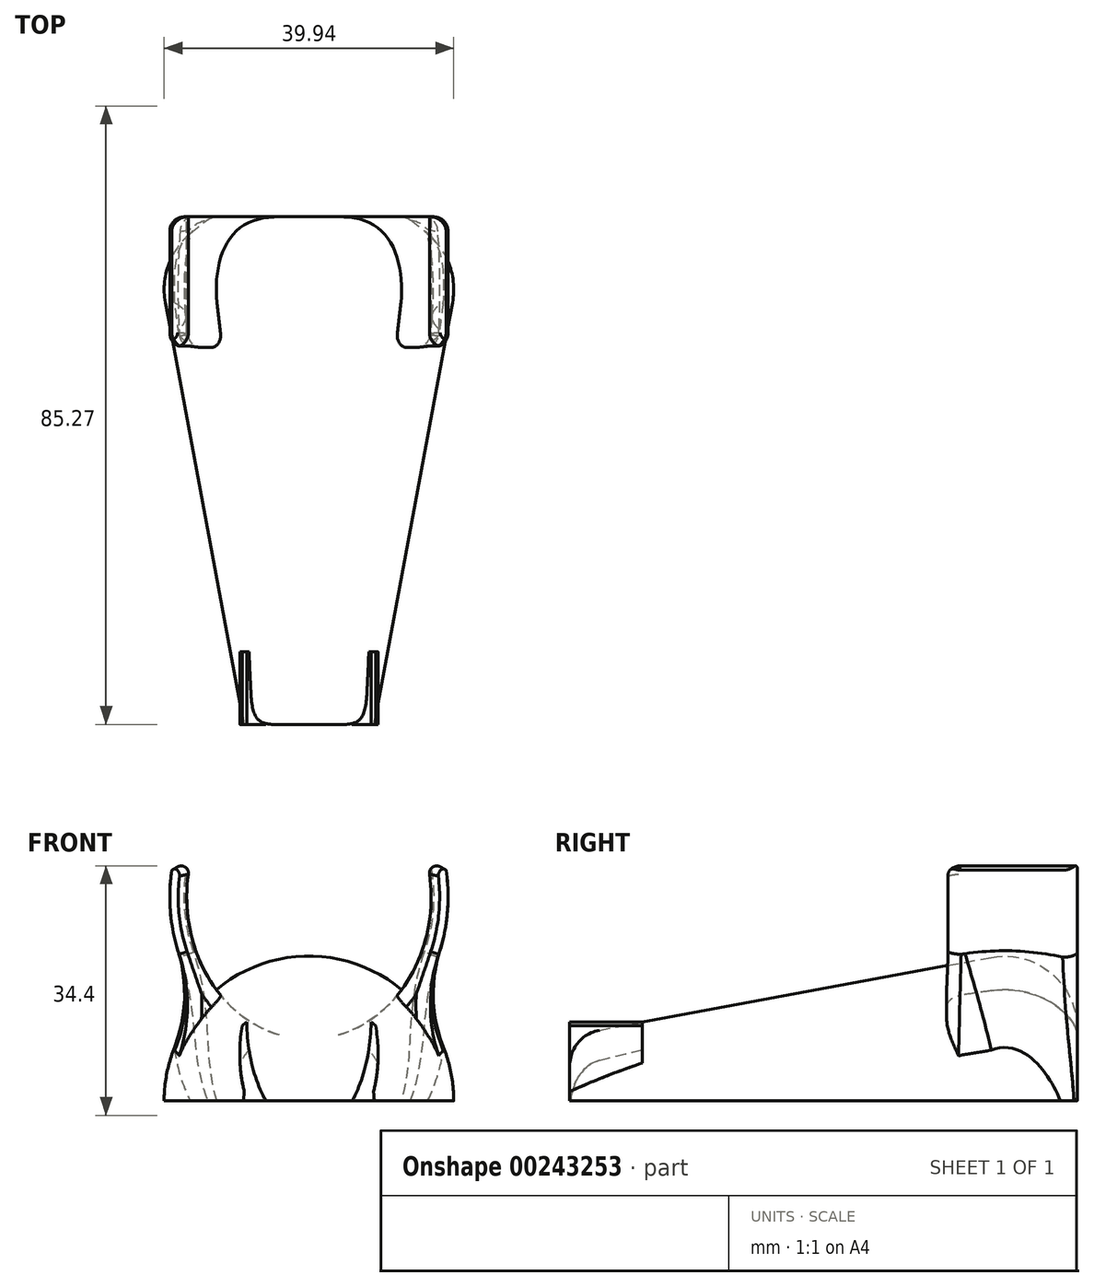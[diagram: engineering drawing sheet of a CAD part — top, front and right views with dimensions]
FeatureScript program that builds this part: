
annotation { "Feature Type Name" : "Feature", "Feature Type Description" : "" }
export const myFeature = defineFeature(function(context is Context, id is Id, definition is map)
    precondition{}
    {
        {
            var Q0;
            Q0=qCreatedBy(makeId("Right.planeOp"),FACE);
            var sketch = newSketch(context, id + "F0", { "sketchPlane" : qUnion([Q0])});
            skLineSegment(sketch, "E0", {"start": v(0, 0) * mm, "end": v(70, 0) * mm});
            skLineSegment(sketch, "E1", {"start": v(0, 0) * mm, "end": v(0, 9) * mm});
            skLineSegment(sketch, "E2", {"start": v(0, 9) * mm, "end": v(70, 22) * mm});
            skLineSegment(sketch, "E3", {"start": v(70, 22) * mm, "end": v(70, 0) * mm});
            skLineSegment(sketch, "E4", {"start": v(0, 0) * mm, "end": v(-40.56, 0) * mm, "construction": true});
            skSolve(sketch);
        }
        {
            var Q0;
            Q0 = qSketchRegion(id + "F0", true);
            var Q1;
            Q1=sQuery(id+"F0.wireOp",EDGE,"E4");
            revolve(context, id + "F1", {"entities" : qUnion([Q0]), "axis" : qUnion([Q1]), "revolveType" : RevolveType.SYMMETRIC, "angle" : 180 * degree});
        }
        {
            var Q0;
            Q0=makeQuery(id+"F1.opRevolve","SWEPT_FACE",FACE,{"disambiguationData":[OSD([sQuery(id+"F0.wireOp",EDGE,"E1")])]});
            var sketch = newSketch(context, id + "F2", { "sketchPlane" : qUnion([Q0])});
            skEllipticalArc(sketch, "E5", {});
            skEllipticalArc(sketch, "E6", {});
            skArc(sketch, "E7", {"start": v(-16.27, 33.26) * mm, "mid": v(-17.6, 32.57) * mm, "end": v(-18.92, 31.83) * mm});
            skArc(sketch, "E8.trimOffspring", {"start": v(18.92, 31.83) * mm, "mid": v(17.6, 32.57) * mm, "end": v(16.27, 33.26) * mm});
            const initialGuessF2  = {"E5": [0, 0.02812500111758709, 0, -1, 0.01959677506238222, 0.016858613568751533, 4.447179239963011, 1.8360060672165754], "E6": [0, 0.02812500111758709, 0, 1, 0.021955648437142372, 0.019191871203235133, 1.4012127593999653, 4.881972547779622]};
            skSetInitialGuess(sketch, initialGuessF2);
            skSolve(sketch);
        }
        {
            var Q0;
            Q0=makeQuery(id+"F1.opRevolve","SWEPT_FACE",FACE,{"disambiguationData":[OSD([sQuery(id+"F0.wireOp",EDGE,"E3")])]});
            var sketch = newSketch(context, id + "F3", { "sketchPlane" : qUnion([Q0])});
            skEllipticalArc(sketch, "E9.0", {});
            skEllipticalArc(sketch, "E9.1", {});
            skPoint(sketch, "E9.2", {"position": v(-16.27, 33.26) * mm});
            skPoint(sketch, "E9.3", {"position": v(-18.92, 31.83) * mm});
            skArc(sketch, "E9.4", {"start": v(-18.92, 31.83) * mm, "mid": v(-17.6, 32.57) * mm, "end": v(-16.27, 33.26) * mm});
            skArc(sketch, "E9.5", {"start": v(16.27, 33.26) * mm, "mid": v(17.6, 32.57) * mm, "end": v(18.92, 31.83) * mm});
            skPoint(sketch, "E9.6", {"position": v(-17.6, 32.57) * mm});
            const initialGuessF3  = {"E9.0": [0, 0.02812500111758709, 0, -1, 0.01959677506238222, 0.016858613568751533, 4.4471792399630115, 1.8360060672165759], "E9.1": [0, 0.02812500111758709, 0, 1, 0.021955648437142372, 0.019191871203235133, 1.4012127593999646, 4.881972547779621]};
            skSetInitialGuess(sketch, initialGuessF3);
            skSolve(sketch);
        }
        {
            var Q0;
            Q0 = qSketchRegion(id + "F3", true);
            extrude(context, id + "F4", {"entities" : qUnion([Q0]), "operationType" : NewBodyOperationType.ADD, "oppositeDirection" : true, "depth" : 18 * mm});
        }
        {
            var Q0;
            {var subQ0=sQuery(id+"F0.wireOp",EDGE,"E2");var subQ1=sQuery(id+"F0.wireOp",EDGE,"E3");var subQ2=sQuery(id+"F3.wireOp",EDGE,"E9.0");Q0=makeQuery(id+"F4.boolean.opBoolean","SPLIT",EDGE,{"disambiguationData":[TD([makeQuery(id+"F1.opRevolve","SWEPT_FACE",FACE,{"disambiguationData":[OSD([subQ0])]}),makeQuery(id+"F1.opRevolve","SWEPT_FACE",FACE,{"disambiguationData":[OSD([subQ1])]}),makeQuery(id+"F4.opExtrude","SWEPT_FACE",FACE,{"disambiguationData":[OSD([subQ2])]}),makeQuery(id+"F4.opExtrude","CAP_FACE",FACE,{"disambiguationData":[OSD([subQ2,sQuery(id+"F3.wireOp",EDGE,"E9.1"),sQuery(id+"F3.wireOp",EDGE,"E9.4"),sQuery(id+"F3.wireOp",EDGE,"E9.5")])],"isStart":true})])],"derivedFrom":makeQuery(id+"F1.opRevolve","SWEPT_EDGE",EDGE,{"disambiguationData":[OSD([subQ0,subQ1])]})});}
            var Q1;
            {var subQ0=sQuery(id+"F3.wireOp",EDGE,"E9.1");var subQ1=sQuery(id+"F0.wireOp",EDGE,"E3");var subQ2=sQuery(id+"F0.wireOp",EDGE,"E2");Q1=makeQuery(id+"F4.boolean.opBoolean","SPLIT",EDGE,{"disambiguationData":[TD([makeQuery(id+"F1.opRevolve","CAP_FACE",FACE,{"disambiguationData":[OSD([sQuery(id+"F0.wireOp",EDGE,"E0"),sQuery(id+"F0.wireOp",EDGE,"E1"),subQ2,subQ1])],"isStart":true}),makeQuery(id+"F1.opRevolve","SWEPT_FACE",FACE,{"disambiguationData":[OSD([subQ2])]}),makeQuery(id+"F1.opRevolve","SWEPT_FACE",FACE,{"disambiguationData":[OSD([subQ1])]}),makeQuery(id+"F4.opExtrude","CAP_FACE",FACE,{"disambiguationData":[OSD([sQuery(id+"F3.wireOp",EDGE,"E9.0"),subQ0,sQuery(id+"F3.wireOp",EDGE,"E9.4"),sQuery(id+"F3.wireOp",EDGE,"E9.5")])],"isStart":true}),makeQuery(id+"F4.opExtrude","SWEPT_FACE",FACE,{"disambiguationData":[OSD([subQ0])]})]),OD(0.0)],"derivedFrom":makeQuery(id+"F1.opRevolve","SWEPT_EDGE",EDGE,{"disambiguationData":[OSD([subQ2,subQ1])]})});}
            var Q2;
            {var subQ0=sQuery(id+"F3.wireOp",EDGE,"E9.1");var subQ1=sQuery(id+"F0.wireOp",EDGE,"E3");var subQ2=sQuery(id+"F0.wireOp",EDGE,"E2");Q2=makeQuery(id+"F4.boolean.opBoolean","SPLIT",EDGE,{"disambiguationData":[TD([makeQuery(id+"F1.opRevolve","CAP_FACE",FACE,{"disambiguationData":[OSD([sQuery(id+"F0.wireOp",EDGE,"E0"),sQuery(id+"F0.wireOp",EDGE,"E1"),subQ2,subQ1])],"isStart":true}),makeQuery(id+"F1.opRevolve","SWEPT_FACE",FACE,{"disambiguationData":[OSD([subQ2])]}),makeQuery(id+"F1.opRevolve","SWEPT_FACE",FACE,{"disambiguationData":[OSD([subQ1])]}),makeQuery(id+"F4.opExtrude","CAP_FACE",FACE,{"disambiguationData":[OSD([sQuery(id+"F3.wireOp",EDGE,"E9.0"),subQ0,sQuery(id+"F3.wireOp",EDGE,"E9.4"),sQuery(id+"F3.wireOp",EDGE,"E9.5")])],"isStart":true}),makeQuery(id+"F4.opExtrude","SWEPT_FACE",FACE,{"disambiguationData":[OSD([subQ0])]})]),OD(1.0)],"derivedFrom":makeQuery(id+"F1.opRevolve","SWEPT_EDGE",EDGE,{"disambiguationData":[OSD([subQ2,subQ1])]})});}
            fillet(context, id + "F5", {"entities" : qUnion([Q0, Q1, Q2]), "radius" : 10 * mm, "tangentPropagation" : true, "allowEdgeOverflow" : false});
        }
        {
            var Q0;
            Q0=makeQuery(id+"F1.opRevolve","SWEPT_FACE",FACE,{"disambiguationData":[OSD([sQuery(id+"F0.wireOp",EDGE,"E1")])]});
            var sketch = newSketch(context, id + "F6", { "sketchPlane" : qUnion([Q0])});
            skEllipticalArc(sketch, "E10", {});
            skPoint(sketch, "E10.centerSnap0", {"position": v(0, 9) * mm});
            skEllipticalArc(sketch, "E11", {});
            skArc(sketch, "E12", {"start": v(-8.6, 10.88) * mm, "mid": v(-8.9, 10.64) * mm, "end": v(-9.19, 10.38) * mm});
            skArc(sketch, "E13.trimOffspring", {"start": v(9.19, 10.38) * mm, "mid": v(8.9, 10.64) * mm, "end": v(8.6, 10.88) * mm});
            skArc(sketch, "E14", {"start": v(-6.72, 1.57) * mm, "mid": v(-7.7, 1) * mm, "end": v(-8.65, 0.34) * mm});
            skEllipticalArc(sketch, "E15.trimOffspring", {});
            skEllipticalArc(sketch, "E16.trimOffspring", {});
            skArc(sketch, "E17.trimOffspring", {"start": v(8.65, 0.34) * mm, "mid": v(7.7, 1) * mm, "end": v(6.72, 1.57) * mm});
            const initialGuessF6  = {"E10": [0, 0.006469425279647112, 0, 1, 0.014514218550175428, 0.009542581655182156, 1.2976381463723867, 2.0065825159044817], "E11": [0, 0.011467698961496353, 0, 1, 0.015859907492995262, 0.008600096534164775, 1.607726325059323, 2.2448390762123314], "E15.trimOffspring": [0, 0.011467698961496353, 0, 1, 0.015859907492995262, 0.008600096534164775, 4.038346230967255, 4.675458982120263], "E16.trimOffspring": [0, 0.006469425279647112, 0, 1, 0.014514218550175428, 0.009542581655182156, 4.276602791275611, 4.985547160807199]};
            skSetInitialGuess(sketch, initialGuessF6);
            skSolve(sketch);
        }
        {
            var Q0;
            Q0 = qSketchRegion(id + "F6", true);
            extrude(context, id + "F7", {"entities" : qUnion([Q0]), "operationType" : NewBodyOperationType.ADD, "oppositeDirection" : true, "depth" : 10 * mm});
        }
        {
            var Q0;
            {var subQ0=sQuery(id+"F6.wireOp",EDGE,"E11");var subQ1=sQuery(id+"F0.wireOp",EDGE,"E2");var subQ3=sQuery(id+"F0.wireOp",EDGE,"E1");Q0=makeQuery(id+"F7.boolean.opBoolean","SPLIT",EDGE,{"disambiguationData":[TD([makeQuery(id+"F7.opExtrude","SWEPT_FACE",FACE,{"disambiguationData":[OSD([subQ0])]})])],"derivedFrom":makeQuery(id+"F1.opRevolve","SWEPT_EDGE",EDGE,{"disambiguationData":[OSD([subQ3,subQ1])]})});}
            fillet(context, id + "F8", {"entities" : qUnion([Q0]), "radius" : 5 * mm, "tangentPropagation" : true, "allowEdgeOverflow" : false});
        }
        {
            var Q0;
            Q0=makeQuery(id+"F4.boolean.opBoolean","INTERSECT",EDGE,{"disambiguationData":[OD(1.0)],"derivedFrom":[makeQuery(id+"F1.opRevolve","SWEPT_FACE",FACE,{"disambiguationData":[OSD([sQuery(id+"F0.wireOp",EDGE,"E2")])]}),makeQuery(id+"F4.opExtrude","SWEPT_FACE",FACE,{"disambiguationData":[OSD([sQuery(id+"F3.wireOp",EDGE,"E9.1")])]})]});
            var Q1;
            Q1=makeQuery(id+"F4.boolean.opBoolean","INTERSECT",EDGE,{"disambiguationData":[OD(0.0)],"derivedFrom":[makeQuery(id+"F1.opRevolve","SWEPT_FACE",FACE,{"disambiguationData":[OSD([sQuery(id+"F0.wireOp",EDGE,"E2")])]}),makeQuery(id+"F4.opExtrude","SWEPT_FACE",FACE,{"disambiguationData":[OSD([sQuery(id+"F3.wireOp",EDGE,"E9.1")])]})]});
            fillet(context, id + "F9", {"entities" : qUnion([Q0, Q1]), "radius" : 20 * mm, "tangentPropagation" : true, "allowEdgeOverflow" : false});
        }
        {
            var Q0;
            {var subQ0=sQuery(id+"F3.wireOp",EDGE,"E9.0");var subQ1=sQuery(id+"F3.wireOp",EDGE,"E9.5");Q0=makeQuery(id+"F4.boolean.opBoolean","SPLIT",EDGE,{"disambiguationData":[TD([makeQuery(id+"F4.opExtrude","SWEPT_FACE",FACE,{"disambiguationData":[OSD([subQ1])]})])],"derivedFrom":makeQuery(id+"F4.opExtrude","CAP_EDGE",EDGE,{"disambiguationData":[OSD([subQ0])],"isStart":false})});}
            var Q1;
            {var subQ0=sQuery(id+"F3.wireOp",EDGE,"E9.0");var subQ1=sQuery(id+"F3.wireOp",EDGE,"E9.4");Q1=makeQuery(id+"F4.boolean.opBoolean","SPLIT",EDGE,{"disambiguationData":[TD([makeQuery(id+"F4.opExtrude","SWEPT_FACE",FACE,{"disambiguationData":[OSD([subQ1])]})])],"derivedFrom":makeQuery(id+"F4.opExtrude","CAP_EDGE",EDGE,{"disambiguationData":[OSD([subQ0])],"isStart":false})});}
            var Q2;
            {var subQ0=sQuery(id+"F3.wireOp",EDGE,"E9.5");var subQ1=sQuery(id+"F3.wireOp",EDGE,"E9.4");var subQ2=sQuery(id+"F3.wireOp",EDGE,"E9.1");var subQ3=sQuery(id+"F3.wireOp",EDGE,"E9.0");var subQ4=makeQuery(id+"F4.opExtrude","CAP_FACE",FACE,{"disambiguationData":[OSD([subQ3,subQ2,subQ1,subQ0])],"isStart":true});var subQ5=sQuery(id+"F0.wireOp",EDGE,"E3");var subQ6=makeQuery(id+"F1.opRevolve","SWEPT_FACE",FACE,{"disambiguationData":[OSD([subQ5])]});var subQ7=sQuery(id+"F0.wireOp",EDGE,"E2");var subQ8=makeQuery(id+"F1.opRevolve","SWEPT_FACE",FACE,{"disambiguationData":[OSD([subQ7])]});var subQ9=makeQuery(id+"F4.opExtrude","SWEPT_FACE",FACE,{"disambiguationData":[OSD([subQ2])]});Q2=makeQuery(id+"F9.opFillet","BLEND_EDGE",EDGE,{"blendedFrom":[makeQuery(id+"F5.opFillet","BLEND_EDGE",EDGE,{"blendedFrom":[makeQuery(id+"F4.boolean.opBoolean","SPLIT",EDGE,{"disambiguationData":[TD([makeQuery(id+"F1.opRevolve","CAP_FACE",FACE,{"disambiguationData":[OSD([sQuery(id+"F0.wireOp",EDGE,"E0"),sQuery(id+"F0.wireOp",EDGE,"E1"),subQ7,subQ5])],"isStart":true}),subQ8,subQ6,subQ4,subQ9]),OD(0.0)],"derivedFrom":makeQuery(id+"F1.opRevolve","SWEPT_EDGE",EDGE,{"disambiguationData":[OSD([subQ7,subQ5])]})}),makeQuery(id+"F4.boolean.opBoolean","SPLIT",FACE,{"disambiguationData":[TD([makeQuery(id+"F4.opExtrude","SWEPT_FACE",FACE,{"disambiguationData":[OSD([subQ1])]})])],"derivedFrom":subQ9})],"blendedInto":[makeQuery(id+"F4.boolean.opBoolean","SPLIT",FACE,{"disambiguationData":[TD([makeQuery(id+"F4.opExtrude","SWEPT_FACE",FACE,{"disambiguationData":[OSD([subQ1])]})])],"derivedFrom":subQ9})]}),makeQuery(id+"F4.boolean.opBoolean","MERGE",FACE,{"derivedFrom":[subQ6,subQ4]})],"blendedInto":[makeQuery(id+"F4.boolean.opBoolean","MERGE",FACE,{"derivedFrom":[subQ6,subQ4]})]});}
            var Q3;
            {var subQ0=sQuery(id+"F3.wireOp",EDGE,"E9.5");var subQ1=sQuery(id+"F3.wireOp",EDGE,"E9.4");var subQ2=sQuery(id+"F3.wireOp",EDGE,"E9.1");var subQ3=sQuery(id+"F3.wireOp",EDGE,"E9.0");var subQ4=makeQuery(id+"F4.opExtrude","CAP_FACE",FACE,{"disambiguationData":[OSD([subQ3,subQ2,subQ1,subQ0])],"isStart":true});var subQ5=sQuery(id+"F0.wireOp",EDGE,"E3");var subQ6=makeQuery(id+"F1.opRevolve","SWEPT_FACE",FACE,{"disambiguationData":[OSD([subQ5])]});var subQ7=sQuery(id+"F0.wireOp",EDGE,"E2");var subQ8=makeQuery(id+"F1.opRevolve","SWEPT_FACE",FACE,{"disambiguationData":[OSD([subQ7])]});var subQ9=makeQuery(id+"F4.opExtrude","SWEPT_FACE",FACE,{"disambiguationData":[OSD([subQ2])]});Q3=makeQuery(id+"F9.opFillet","BLEND_EDGE",EDGE,{"blendedFrom":[makeQuery(id+"F5.opFillet","BLEND_EDGE",EDGE,{"blendedFrom":[makeQuery(id+"F4.boolean.opBoolean","SPLIT",EDGE,{"disambiguationData":[TD([makeQuery(id+"F1.opRevolve","CAP_FACE",FACE,{"disambiguationData":[OSD([sQuery(id+"F0.wireOp",EDGE,"E0"),sQuery(id+"F0.wireOp",EDGE,"E1"),subQ7,subQ5])],"isStart":true}),subQ8,subQ6,subQ4,subQ9]),OD(1.0)],"derivedFrom":makeQuery(id+"F1.opRevolve","SWEPT_EDGE",EDGE,{"disambiguationData":[OSD([subQ7,subQ5])]})}),makeQuery(id+"F4.boolean.opBoolean","SPLIT",FACE,{"disambiguationData":[TD([makeQuery(id+"F4.opExtrude","SWEPT_FACE",FACE,{"disambiguationData":[OSD([subQ0])]})])],"derivedFrom":subQ9})],"blendedInto":[makeQuery(id+"F4.boolean.opBoolean","SPLIT",FACE,{"disambiguationData":[TD([makeQuery(id+"F4.opExtrude","SWEPT_FACE",FACE,{"disambiguationData":[OSD([subQ0])]})])],"derivedFrom":subQ9})]}),makeQuery(id+"F4.boolean.opBoolean","MERGE",FACE,{"derivedFrom":[subQ6,subQ4]})],"blendedInto":[makeQuery(id+"F4.boolean.opBoolean","MERGE",FACE,{"derivedFrom":[subQ6,subQ4]})]});}
            var Q4;
            {var subQ0=makeQuery(id+"F1.opRevolve","SWEPT_FACE",FACE,{"disambiguationData":[OSD([sQuery(id+"F0.wireOp",EDGE,"E2")])]});var subQ1=sQuery(id+"F3.wireOp",EDGE,"E9.0");var subQ2=sQuery(id+"F3.wireOp",EDGE,"E9.5");var subQ3=sQuery(id+"F3.wireOp",EDGE,"E9.1");var subQ4=makeQuery(id+"F4.opExtrude","SWEPT_FACE",FACE,{"disambiguationData":[OSD([subQ3])]});Q4=makeQuery(id+"F9.opFillet","BLEND_EDGE",EDGE,{"blendedFrom":[makeQuery(id+"F4.boolean.opBoolean","INTERSECT",EDGE,{"disambiguationData":[OD(1.0)],"derivedFrom":[subQ0,subQ4]}),makeQuery(id+"F4.boolean.opBoolean","SPLIT",FACE,{"disambiguationData":[TD([makeQuery(id+"F4.opExtrude","SWEPT_FACE",FACE,{"disambiguationData":[OSD([subQ2])]})])],"derivedFrom":makeQuery(id+"F4.opExtrude","CAP_FACE",FACE,{"disambiguationData":[OSD([subQ1,subQ3,sQuery(id+"F3.wireOp",EDGE,"E9.4"),subQ2])],"isStart":false})})],"blendedInto":[makeQuery(id+"F4.boolean.opBoolean","SPLIT",FACE,{"disambiguationData":[TD([makeQuery(id+"F4.opExtrude","SWEPT_FACE",FACE,{"disambiguationData":[OSD([subQ2])]})])],"derivedFrom":makeQuery(id+"F4.opExtrude","CAP_FACE",FACE,{"disambiguationData":[OSD([subQ1,subQ3,sQuery(id+"F3.wireOp",EDGE,"E9.4"),subQ2])],"isStart":false})})]});}
            var Q5;
            {var subQ0=makeQuery(id+"F1.opRevolve","SWEPT_FACE",FACE,{"disambiguationData":[OSD([sQuery(id+"F0.wireOp",EDGE,"E2")])]});var subQ1=sQuery(id+"F3.wireOp",EDGE,"E9.0");var subQ2=sQuery(id+"F3.wireOp",EDGE,"E9.4");var subQ3=sQuery(id+"F3.wireOp",EDGE,"E9.1");var subQ4=makeQuery(id+"F4.opExtrude","SWEPT_FACE",FACE,{"disambiguationData":[OSD([subQ3])]});Q5=makeQuery(id+"F9.opFillet","BLEND_EDGE",EDGE,{"blendedFrom":[makeQuery(id+"F4.boolean.opBoolean","INTERSECT",EDGE,{"disambiguationData":[OD(0.0)],"derivedFrom":[subQ0,subQ4]}),makeQuery(id+"F4.boolean.opBoolean","SPLIT",FACE,{"disambiguationData":[TD([makeQuery(id+"F4.opExtrude","SWEPT_FACE",FACE,{"disambiguationData":[OSD([subQ2])]})])],"derivedFrom":makeQuery(id+"F4.opExtrude","CAP_FACE",FACE,{"disambiguationData":[OSD([subQ1,subQ3,subQ2,sQuery(id+"F3.wireOp",EDGE,"E9.5")])],"isStart":false})})],"blendedInto":[makeQuery(id+"F4.boolean.opBoolean","SPLIT",FACE,{"disambiguationData":[TD([makeQuery(id+"F4.opExtrude","SWEPT_FACE",FACE,{"disambiguationData":[OSD([subQ2])]})])],"derivedFrom":makeQuery(id+"F4.opExtrude","CAP_FACE",FACE,{"disambiguationData":[OSD([subQ1,subQ3,subQ2,sQuery(id+"F3.wireOp",EDGE,"E9.5")])],"isStart":false})})]});}
            fillet(context, id + "F10", {"entities" : qUnion([Q0, Q1, Q2, Q3, Q4, Q5]), "radius" : 2 * mm, "tangentPropagation" : true, "allowEdgeOverflow" : false});
        }
        {
            var Q0;
            Q0=makeQuery(id+"F4.opExtrude","SWEPT_EDGE",EDGE,{"disambiguationData":[OSD([sQuery(id+"F3.wireOp",EDGE,"E9.0"),sQuery(id+"F3.wireOp",EDGE,"E9.4")])]});
            var Q1;
            Q1=makeQuery(id+"F4.opExtrude","SWEPT_EDGE",EDGE,{"disambiguationData":[OSD([sQuery(id+"F3.wireOp",EDGE,"E9.0"),sQuery(id+"F3.wireOp",EDGE,"E9.5")])]});
            fillet(context, id + "F11", {"entities" : qUnion([Q0, Q1]), "radius" : 1 * mm, "tangentPropagation" : true, "allowEdgeOverflow" : false});
        }
    });
